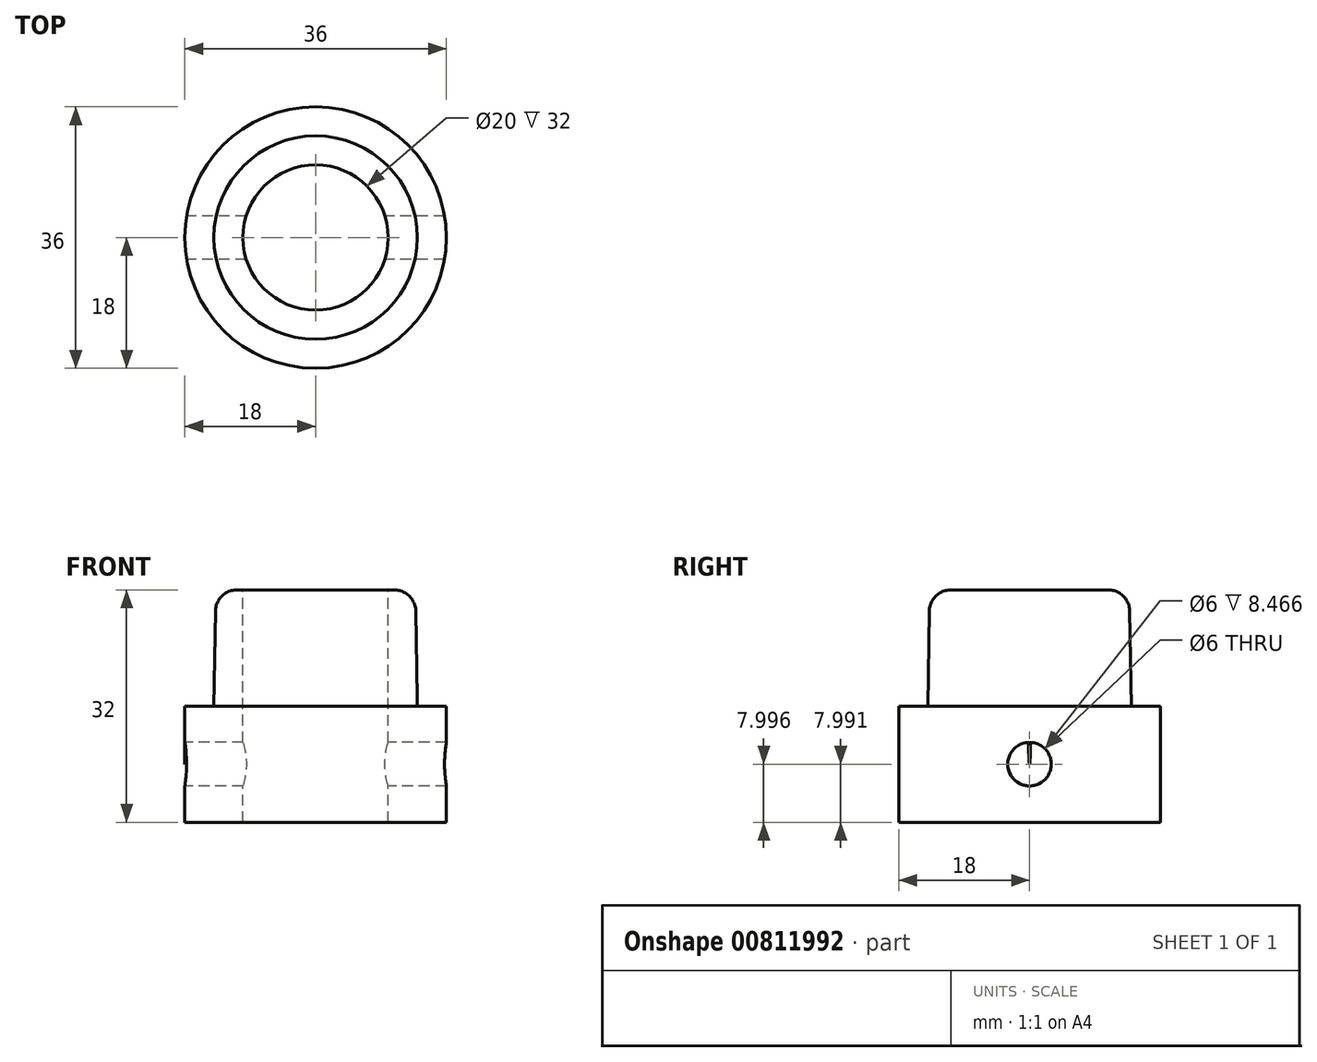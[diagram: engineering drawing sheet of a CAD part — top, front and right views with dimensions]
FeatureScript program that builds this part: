
annotation { "Feature Type Name" : "Feature", "Feature Type Description" : "" }
export const myFeature = defineFeature(function(context is Context, id is Id, definition is map)
    precondition{}
    {
        {
            var Q0;
            Q0=qCreatedBy(makeId("Front.planeOp"),FACE);
            var sketch = newSketch(context, id + "F0", { "sketchPlane" : qUnion([Q0])});
            skLineSegment(sketch, "E0", {"start": v(0, 62.68) * mm, "end": v(0, -76.65) * mm, "construction": true});
            skLineSegment(sketch, "E1", {"start": v(-10, 16) * mm, "end": v(-10, -16) * mm});
            skLineSegment(sketch, "E2", {"start": v(-10, 16) * mm, "end": v(-13.75, 16) * mm});
            skLineSegment(sketch, "E3", {"start": v(-13.75, 16) * mm, "end": v(-14, 0) * mm});
            skLineSegment(sketch, "E4", {"start": v(-14, 0) * mm, "end": v(-18, 0) * mm});
            skLineSegment(sketch, "E5", {"start": v(-18, 0) * mm, "end": v(-18, -16) * mm});
            skLineSegment(sketch, "E6", {"start": v(-18, -16) * mm, "end": v(-10, -16) * mm});
            skPoint(sketch, "E7", {"position": v(-18, -8) * mm});
            skSolve(sketch);
        }
        {
            var Q0;
            Q0 = qSketchRegion(id + "F0", true);
            var Q1;
            Q1=sQuery(id+"F0.wireOp",EDGE,"E0");
            revolve(context, id + "F1", {"surfaceOperationType" : NewSurfaceOperationType.NEW, "entities" : qUnion([Q0]), "axis" : qUnion([Q1]), "revolveType" : RevolveType.FULL});
        }
        {
            var Q0;
            Q0=sQuery(id+"F0.wireOp",EDGE,"E5");
            cPoint(context, id + "F2", {"entities" : qUnion([Q0]), "parameter" : 0.5});
        }
        {
            var Q0;
            Q0 = qCreatedBy(id + "F2" ,VERTEX);
            var Q1;
            Q1=sQuery(id+"F0.wireOp",EDGE,"E6");
            cPlane(context, id + "F3", {"entities" : qUnion([Q0, Q1]), "cplaneType" : CPlaneType.LINE_POINT, "offset" : 25 * mm, "width" : 150 * mm, "height" : 150 * mm});
        }
        {
            var Q0;
            Q0=qCreatedBy(id+"F3.planeOp",FACE);
            var sketch = newSketch(context, id + "F4", { "sketchPlane" : qUnion([Q0])});
            skPoint(sketch, "E8.0", {"position": v(0, -8) * mm});
            skCircle(sketch, "E9", {"center": v(0, -8) * mm, "radius": 3 * mm});
            skSolve(sketch);
        }
        {
            var Q0;
            Q0 = qSketchRegion(id + "F4", true);
            extrude(context, id + "F5", {"entities" : qUnion([Q0]), "operationType" : NewBodyOperationType.REMOVE, "endBound" : BoundingType.THROUGH_ALL, "depth" : 25 * mm, "offsetDistance" : 25 * mm});
        }
        {
            var Q0;
            Q0=makeQuery(id+"F1.opRevolve","SWEPT_EDGE",EDGE,{"disambiguationData":[OSD([sQuery(id+"F0.wireOp",EDGE,"E2"),sQuery(id+"F0.wireOp",EDGE,"E3")])]});
            fillet(context, id + "F6", {"entities" : qUnion([Q0]), "radius" : 3 * mm, "tangentPropagation" : true, "allowEdgeOverflow" : false});
        }
    });
